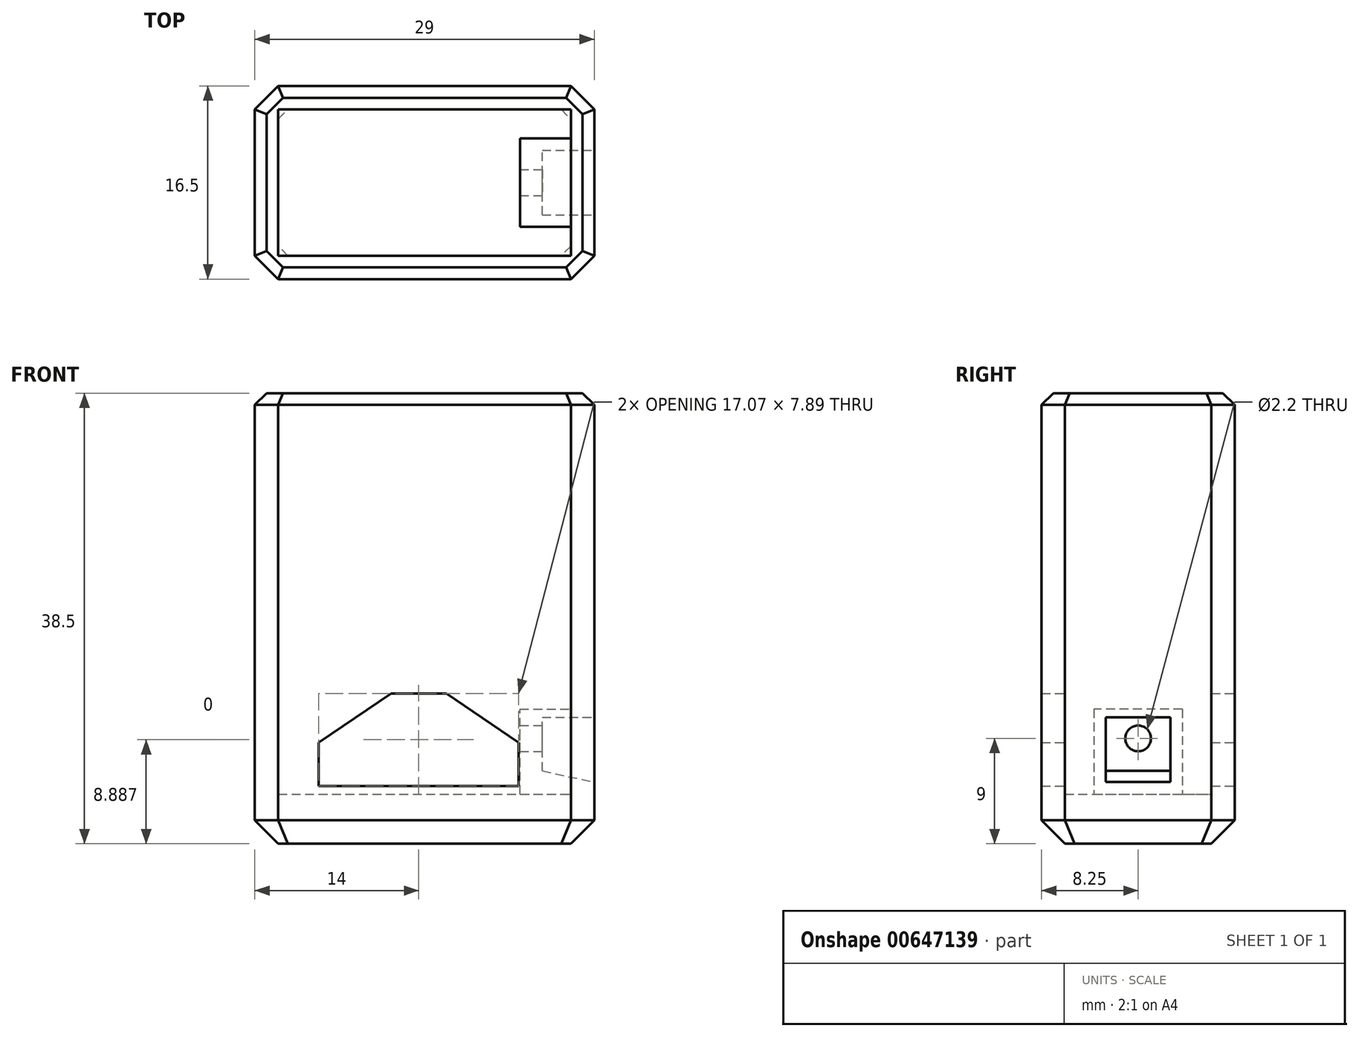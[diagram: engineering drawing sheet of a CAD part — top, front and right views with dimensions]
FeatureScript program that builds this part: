
annotation { "Feature Type Name" : "Feature", "Feature Type Description" : "" }
export const myFeature = defineFeature(function(context is Context, id is Id, definition is map)
    precondition{}
    {
        {
            var Q0;
            Q0=qCreatedBy(makeId("Top.planeOp"),FACE);
            var sketch = newSketch(context, id + "F0", { "sketchPlane" : qUnion([Q0])});
            skLineSegment(sketch, "E0.bottom", {"start": v(0, 0) * mm, "end": v(29, 0) * mm});
            skLineSegment(sketch, "E0.top", {"start": v(0, 16.5) * mm, "end": v(29, 16.5) * mm});
            skLineSegment(sketch, "E0.left", {"start": v(0, 0) * mm, "end": v(0, 16.5) * mm});
            skLineSegment(sketch, "E0.right", {"start": v(29, 0) * mm, "end": v(29, 16.5) * mm});
            skSolve(sketch);
        }
        {
            var Q0;
            Q0=makeQuery(id+"F0.imprint","IMPRINT",FACE,{"disambiguationData":[TD([[makeQuery(id+"F0.imprint","IMPRINT",EDGE,{"derivedFrom":sQuery(id+"F0.wireOp",EDGE,"E0.bottom")}),1.0]])]});
            extrude(context, id + "F1", {"entities" : qUnion([Q0]), "depth" : 38.5 * mm, "offsetDistance" : 25 * mm});
        }
        {
            var Q0;
            Q0=makeQuery(id+"F1.opExtrude","CAP_FACE",FACE,{"disambiguationData":[OSD([sQuery(id+"F0.wireOp",EDGE,"E0.bottom"),sQuery(id+"F0.wireOp",EDGE,"E0.top"),sQuery(id+"F0.wireOp",EDGE,"E0.left"),sQuery(id+"F0.wireOp",EDGE,"E0.right")])],"isStart":false});
            shell(context, id + "F2", {"entities" : qUnion([Q0]), "thickness" : 2 * mm});
        }
        {
            var Q0;
            Q0=makeQuery(id+"F2.opShell","OFFSET_FACE",FACE,{"disambiguationData":[OSD([sQuery(id+"F0.wireOp",EDGE,"E0.bottom"),sQuery(id+"F0.wireOp",EDGE,"E0.top"),sQuery(id+"F0.wireOp",EDGE,"E0.left"),sQuery(id+"F0.wireOp",EDGE,"E0.right")])]});
            extrude(context, id + "F3", {"entities" : qUnion([Q0]), "operationType" : NewBodyOperationType.ADD, "depth" : 2.25 * mm, "offsetDistance" : 25 * mm});
        }
        {
            var Q0;
            Q0=makeQuery(id+"F1.opExtrude","SWEPT_EDGE",EDGE,{"disambiguationData":[OSD([sQuery(id+"F0.wireOp",EDGE,"E0.bottom"),sQuery(id+"F0.wireOp",EDGE,"E0.right")])]});
            var Q1;
            Q1=makeQuery(id+"F1.opExtrude","SWEPT_EDGE",EDGE,{"disambiguationData":[OSD([sQuery(id+"F0.wireOp",EDGE,"E0.top"),sQuery(id+"F0.wireOp",EDGE,"E0.right")])]});
            var Q2;
            Q2=makeQuery(id+"F1.opExtrude","SWEPT_EDGE",EDGE,{"disambiguationData":[OSD([sQuery(id+"F0.wireOp",EDGE,"E0.bottom"),sQuery(id+"F0.wireOp",EDGE,"E0.left")])]});
            var Q3;
            Q3=makeQuery(id+"F1.opExtrude","SWEPT_EDGE",EDGE,{"disambiguationData":[OSD([sQuery(id+"F0.wireOp",EDGE,"E0.top"),sQuery(id+"F0.wireOp",EDGE,"E0.left")])]});
            chamfer(context, id + "F4", {"entities" : qUnion([Q0, Q1, Q2, Q3]), "width" : 2 * mm, "tangentPropagation" : true});
        }
        {
            var Q0;
            Q0=makeQuery(id+"F1.opExtrude","CAP_FACE",FACE,{"disambiguationData":[OSD([sQuery(id+"F0.wireOp",EDGE,"E0.bottom"),sQuery(id+"F0.wireOp",EDGE,"E0.top"),sQuery(id+"F0.wireOp",EDGE,"E0.left"),sQuery(id+"F0.wireOp",EDGE,"E0.right")])],"isStart":true});
            chamfer(context, id + "F5", {"entities" : qUnion([Q0]), "width" : 2 * mm, "tangentPropagation" : true});
        }
        {
            var Q0;
            Q0=makeQuery(id+"F1.opExtrude","CAP_EDGE",EDGE,{"disambiguationData":[OSD([sQuery(id+"F0.wireOp",EDGE,"E0.right")])],"isStart":false});
            var Q1;
            {var subQ0=sQuery(id+"F0.wireOp",EDGE,"E0.right");var subQ1=sQuery(id+"F0.wireOp",EDGE,"E0.bottom");Q1=makeQuery(id+"F4.opChamfer","BLEND_EDGE",EDGE,{"blendedFrom":[makeQuery(id+"F1.opExtrude","SWEPT_EDGE",EDGE,{"disambiguationData":[OSD([subQ1,subQ0])]}),makeQuery(id+"F1.opExtrude","CAP_FACE",FACE,{"disambiguationData":[OSD([subQ1,sQuery(id+"F0.wireOp",EDGE,"E0.top"),sQuery(id+"F0.wireOp",EDGE,"E0.left"),subQ0])],"isStart":false})],"blendedInto":[makeQuery(id+"F1.opExtrude","CAP_FACE",FACE,{"disambiguationData":[OSD([subQ1,sQuery(id+"F0.wireOp",EDGE,"E0.top"),sQuery(id+"F0.wireOp",EDGE,"E0.left"),subQ0])],"isStart":false})]});}
            var Q2;
            Q2=makeQuery(id+"F1.opExtrude","CAP_EDGE",EDGE,{"disambiguationData":[OSD([sQuery(id+"F0.wireOp",EDGE,"E0.bottom")])],"isStart":false});
            var Q3;
            {var subQ0=sQuery(id+"F0.wireOp",EDGE,"E0.left");var subQ1=sQuery(id+"F0.wireOp",EDGE,"E0.bottom");Q3=makeQuery(id+"F4.opChamfer","BLEND_EDGE",EDGE,{"blendedFrom":[makeQuery(id+"F1.opExtrude","SWEPT_EDGE",EDGE,{"disambiguationData":[OSD([subQ1,subQ0])]}),makeQuery(id+"F1.opExtrude","CAP_FACE",FACE,{"disambiguationData":[OSD([subQ1,sQuery(id+"F0.wireOp",EDGE,"E0.top"),subQ0,sQuery(id+"F0.wireOp",EDGE,"E0.right")])],"isStart":false})],"blendedInto":[makeQuery(id+"F1.opExtrude","CAP_FACE",FACE,{"disambiguationData":[OSD([subQ1,sQuery(id+"F0.wireOp",EDGE,"E0.top"),subQ0,sQuery(id+"F0.wireOp",EDGE,"E0.right")])],"isStart":false})]});}
            var Q4;
            Q4=makeQuery(id+"F1.opExtrude","CAP_EDGE",EDGE,{"disambiguationData":[OSD([sQuery(id+"F0.wireOp",EDGE,"E0.left")])],"isStart":false});
            var Q5;
            {var subQ0=sQuery(id+"F0.wireOp",EDGE,"E0.left");var subQ1=sQuery(id+"F0.wireOp",EDGE,"E0.top");Q5=makeQuery(id+"F4.opChamfer","BLEND_EDGE",EDGE,{"blendedFrom":[makeQuery(id+"F1.opExtrude","SWEPT_EDGE",EDGE,{"disambiguationData":[OSD([subQ1,subQ0])]}),makeQuery(id+"F1.opExtrude","CAP_FACE",FACE,{"disambiguationData":[OSD([sQuery(id+"F0.wireOp",EDGE,"E0.bottom"),subQ1,subQ0,sQuery(id+"F0.wireOp",EDGE,"E0.right")])],"isStart":false})],"blendedInto":[makeQuery(id+"F1.opExtrude","CAP_FACE",FACE,{"disambiguationData":[OSD([sQuery(id+"F0.wireOp",EDGE,"E0.bottom"),subQ1,subQ0,sQuery(id+"F0.wireOp",EDGE,"E0.right")])],"isStart":false})]});}
            var Q6;
            Q6=makeQuery(id+"F1.opExtrude","CAP_EDGE",EDGE,{"disambiguationData":[OSD([sQuery(id+"F0.wireOp",EDGE,"E0.top")])],"isStart":false});
            var Q7;
            {var subQ0=sQuery(id+"F0.wireOp",EDGE,"E0.right");var subQ1=sQuery(id+"F0.wireOp",EDGE,"E0.top");Q7=makeQuery(id+"F4.opChamfer","BLEND_EDGE",EDGE,{"blendedFrom":[makeQuery(id+"F1.opExtrude","SWEPT_EDGE",EDGE,{"disambiguationData":[OSD([subQ1,subQ0])]}),makeQuery(id+"F1.opExtrude","CAP_FACE",FACE,{"disambiguationData":[OSD([sQuery(id+"F0.wireOp",EDGE,"E0.bottom"),subQ1,sQuery(id+"F0.wireOp",EDGE,"E0.left"),subQ0])],"isStart":false})],"blendedInto":[makeQuery(id+"F1.opExtrude","CAP_FACE",FACE,{"disambiguationData":[OSD([sQuery(id+"F0.wireOp",EDGE,"E0.bottom"),subQ1,sQuery(id+"F0.wireOp",EDGE,"E0.left"),subQ0])],"isStart":false})]});}
            chamfer(context, id + "F6", {"entities" : qUnion([Q0, Q1, Q2, Q3, Q4, Q5, Q6, Q7]), "width" : 1 * mm, "tangentPropagation" : true});
        }
        {
            var Q0;
            Q0=makeQuery(id+"F1.opExtrude","SWEPT_FACE",FACE,{"disambiguationData":[OSD([sQuery(id+"F0.wireOp",EDGE,"E0.top")])]});
            var sketch = newSketch(context, id + "F7", { "sketchPlane" : qUnion([Q0])});
            skLineSegment(sketch, "E1", {"start": v(-22.54, 4.94) * mm, "end": v(-5.46, 4.94) * mm});
            skLineSegment(sketch, "E2", {"start": v(-5.46, 4.94) * mm, "end": v(-5.46, 8.66) * mm});
            skLineSegment(sketch, "E3", {"start": v(-5.46, 8.66) * mm, "end": v(-11.64, 12.83) * mm});
            skLineSegment(sketch, "E4", {"start": v(-11.63, 12.83) * mm, "end": v(-16.37, 12.83) * mm});
            skLineSegment(sketch, "E5", {"start": v(-16.36, 12.83) * mm, "end": v(-22.54, 8.66) * mm});
            skLineSegment(sketch, "E6", {"start": v(-22.54, 8.66) * mm, "end": v(-22.54, 4.94) * mm});
            skSolve(sketch);
        }
        {
            var Q0;
            Q0=makeQuery(id+"F7.imprint","IMPRINT",FACE,{"disambiguationData":[TD([[makeQuery(id+"F7.imprint","IMPRINT",EDGE,{"derivedFrom":sQuery(id+"F7.wireOp",EDGE,"E1")}),1.0]])]});
            extrude(context, id + "F8", {"entities" : qUnion([Q0]), "operationType" : NewBodyOperationType.REMOVE, "endBound" : BoundingType.THROUGH_ALL, "oppositeDirection" : true, "depth" : 25 * mm, "offsetDistance" : 25 * mm});
        }
        {
            var Q0;
            Q0=makeQuery(id+"F1.opExtrude","SWEPT_FACE",FACE,{"disambiguationData":[OSD([sQuery(id+"F0.wireOp",EDGE,"E0.right")])]});
            var sketch = newSketch(context, id + "F9", { "sketchPlane" : qUnion([Q0])});
            skLineSegment(sketch, "E7.bottom", {"start": v(4.48, 4.25) * mm, "end": v(12.02, 4.25) * mm});
            skLineSegment(sketch, "E7.top", {"start": v(4.48, 11.5) * mm, "end": v(12.02, 11.5) * mm});
            skLineSegment(sketch, "E7.left", {"start": v(4.48, 4.25) * mm, "end": v(4.48, 11.5) * mm});
            skLineSegment(sketch, "E7.right", {"start": v(12.02, 4.25) * mm, "end": v(12.02, 11.5) * mm});
            skCircle(sketch, "E8", {"center": v(8.25, 9) * mm, "radius": 1.1 * mm});
            skSolve(sketch);
        }
        {
            var Q0;
            Q0=makeQuery(id+"F9.imprint","IMPRINT",FACE,{"disambiguationData":[TD([[makeQuery(id+"F9.imprint","IMPRINT",EDGE,{"derivedFrom":sQuery(id+"F9.wireOp",EDGE,"E7.bottom")}),1.0]])]});
            extrude(context, id + "F10", {"entities" : qUnion([Q0]), "operationType" : NewBodyOperationType.ADD, "oppositeDirection" : true, "depth" : 6.35 * mm, "offsetDistance" : 25 * mm});
        }
        {
            var Q0;
            Q0=makeQuery(id+"F1.opExtrude","SWEPT_FACE",FACE,{"disambiguationData":[OSD([sQuery(id+"F0.wireOp",EDGE,"E0.right")])]});
            var sketch = newSketch(context, id + "F11", { "sketchPlane" : qUnion([Q0])});
            skLineSegment(sketch, "E9.bottom", {"start": v(5.48, 5.27) * mm, "end": v(11.02, 5.27) * mm});
            skLineSegment(sketch, "E9.top", {"start": v(5.48, 10.8) * mm, "end": v(11.02, 10.8) * mm});
            skLineSegment(sketch, "E9.left", {"start": v(5.48, 5.27) * mm, "end": v(5.48, 10.8) * mm});
            skLineSegment(sketch, "E9.right", {"start": v(11.02, 5.27) * mm, "end": v(11.02, 10.8) * mm});
            skSolve(sketch);
        }
        {
            var Q0;
            Q0=makeQuery(id+"F11.imprint","IMPRINT",FACE,{"disambiguationData":[TD([[makeQuery(id+"F11.imprint","IMPRINT",EDGE,{"derivedFrom":sQuery(id+"F11.wireOp",EDGE,"E9.bottom")}),-1.0]])]});
            cPlane(context, id + "F12", {"entities" : qUnion([Q0]), "cplaneType" : CPlaneType.OFFSET, "offset" : 4.45 * mm, "oppositeDirection" : true, "width" : 150 * mm, "height" : 150 * mm});
        }
        {
            var Q0;
            Q0=qCreatedBy(id+"F12.planeOp",FACE);
            var sketch = newSketch(context, id + "F13", { "sketchPlane" : qUnion([Q0])});
            skLineSegment(sketch, "E10.bottom", {"start": v(5.48, 6.22) * mm, "end": v(11.02, 6.22) * mm});
            skLineSegment(sketch, "E10.top", {"start": v(5.48, 10.8) * mm, "end": v(11.02, 10.8) * mm});
            skLineSegment(sketch, "E10.left", {"start": v(5.48, 6.22) * mm, "end": v(5.48, 10.8) * mm});
            skLineSegment(sketch, "E10.right", {"start": v(11.02, 6.22) * mm, "end": v(11.02, 10.8) * mm});
            skSolve(sketch);
        }
        {
            var Q1;
            Q1=qSketchRegion(id+"F13",true);
            var Q2;
            Q2=qSketchRegion(id+"F11",true);
            loft(context, id + "F14", {"operationType" : NewBodyOperationType.REMOVE, "sheetProfilesArray" : [{ "sheetProfileEntities" : qUnion([Q1]) }, { "sheetProfileEntities" : qUnion([Q2]) }]});
        }
    });
